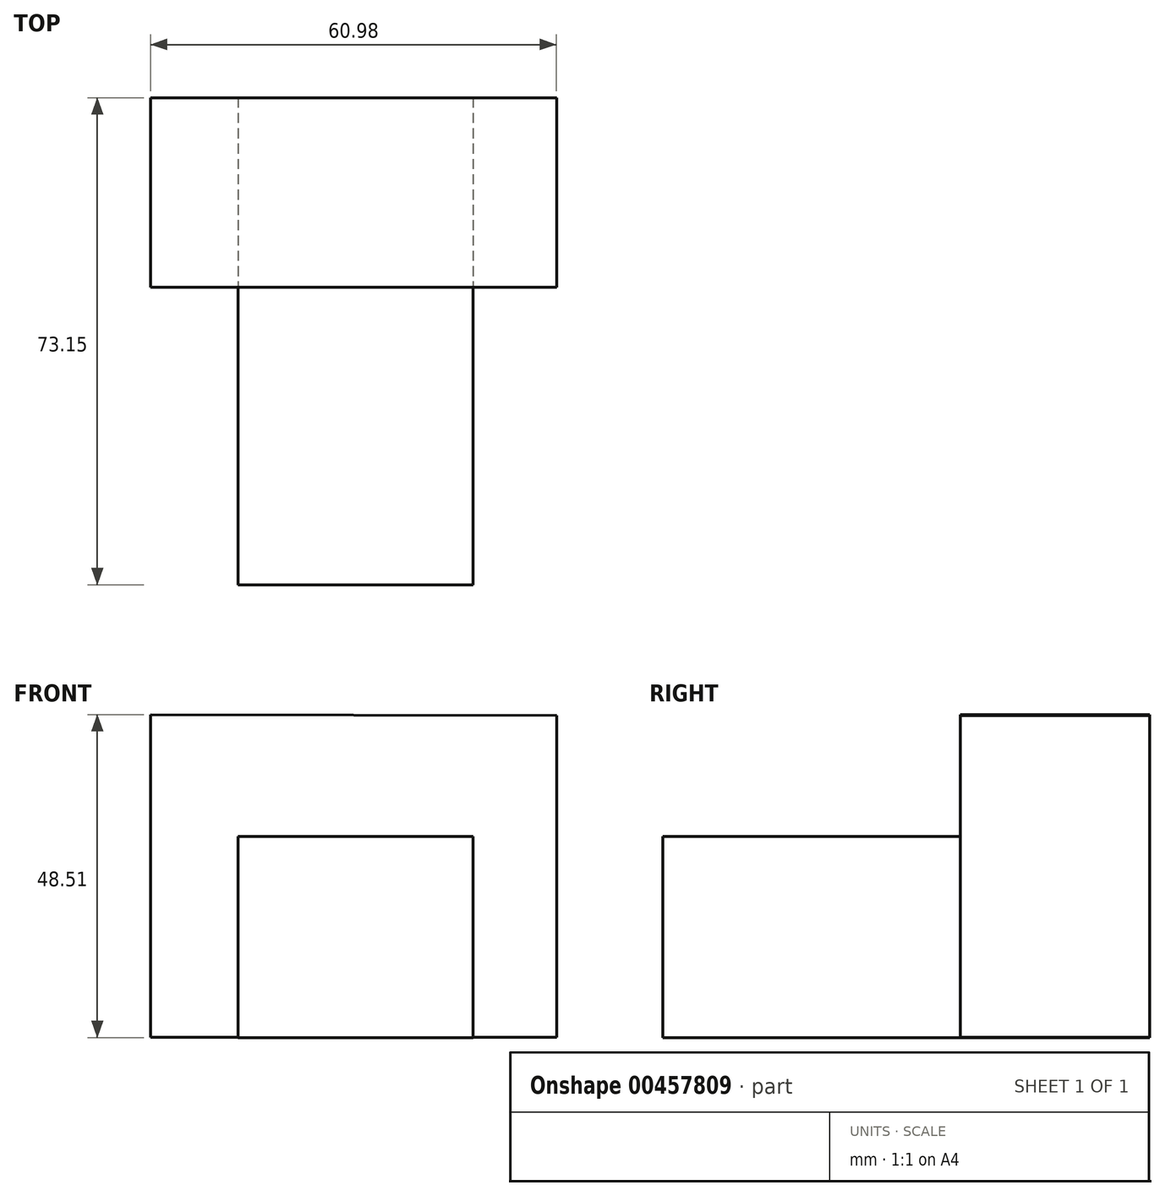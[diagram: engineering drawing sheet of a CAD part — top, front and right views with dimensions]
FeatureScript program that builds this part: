
annotation { "Feature Type Name" : "Feature", "Feature Type Description" : "" }
export const myFeature = defineFeature(function(context is Context, id is Id, definition is map)
    precondition{}
    {
        {
            var Q0;
            Q0=qCreatedBy(makeId("Front.planeOp"),FACE);
            var sketch = newSketch(context, id + "F0", { "sketchPlane" : qUnion([Q0])});
            skLineSegment(sketch, "E0", {"start": v(-39.26, 32.18) * mm, "end": v(-39.26, -16.27) * mm});
            skLineSegment(sketch, "E1", {"start": v(-39.26, -16.27) * mm, "end": v(21.72, -16.27) * mm});
            skLineSegment(sketch, "E2", {"start": v(21.72, -16.27) * mm, "end": v(21.72, 32.06) * mm});
            skLineSegment(sketch, "E3", {"start": v(-39.26, 32.18) * mm, "end": v(21.72, 32.06) * mm});
            skSolve(sketch);
        }
        {
            var Q0;
            Q0=makeQuery(id+"F0.imprint","IMPRINT",FACE,{"disambiguationData":[TD([[makeQuery(id+"F0.imprint","IMPRINT",EDGE,{"derivedFrom":sQuery(id+"F0.wireOp",EDGE,"E0")}),1.0]])]});
            var Q1;
            Q1 = qSketchRegion(id + "F2", true);
            extrude(context, id + "F1", {"entities" : qUnion([Q0, Q1]), "depth" : 28.45 * mm});
        }
        {
            var Q0;
            Q0=qCreatedBy(makeId("Front.planeOp"),FACE);
            var sketch = newSketch(context, id + "F2", { "sketchPlane" : qUnion([Q0])});
            skLineSegment(sketch, "E4", {"start": v(-38.98, -16.33) * mm, "end": v(-26.13, -16.33) * mm});
            skLineSegment(sketch, "E5", {"start": v(-26.13, -16.33) * mm, "end": v(9.18, -16.33) * mm});
            skLineSegment(sketch, "E6", {"start": v(-26.13, -16.33) * mm, "end": v(-26.13, 13.88) * mm});
            skLineSegment(sketch, "E7", {"start": v(-26.13, 13.88) * mm, "end": v(9.18, 13.88) * mm});
            skLineSegment(sketch, "E8", {"start": v(9.18, -16.33) * mm, "end": v(9.18, 13.88) * mm});
            skSolve(sketch);
        }
        {
            var Q0;
            Q0 = qSketchRegion(id + "F2", true);
            extrude(context, id + "F3", {"entities" : qUnion([Q0]), "operationType" : NewBodyOperationType.ADD, "depth" : 73.15 * mm});
        }
    });
